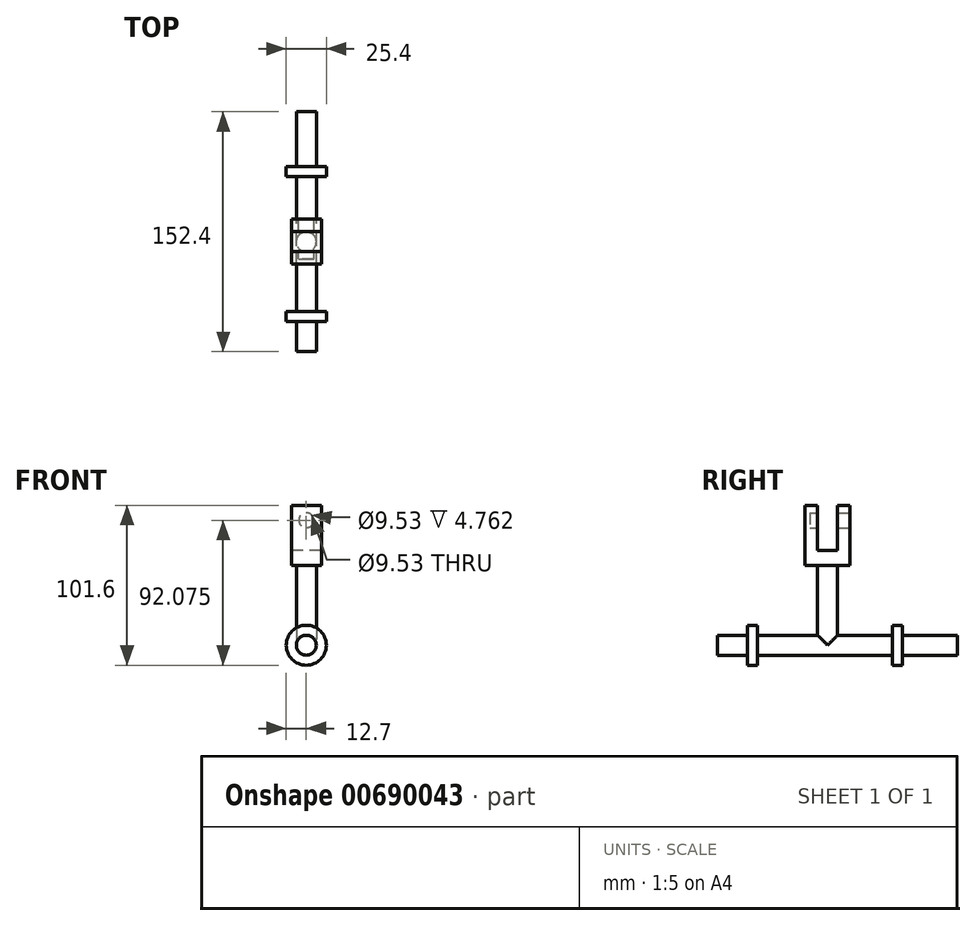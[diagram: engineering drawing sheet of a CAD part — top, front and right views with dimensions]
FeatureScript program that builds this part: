
annotation { "Feature Type Name" : "Feature", "Feature Type Description" : "" }
export const myFeature = defineFeature(function(context is Context, id is Id, definition is map)
    precondition{}
    {
        {
            var Q0;
            Q0=qCreatedBy(makeId("Front.planeOp"),FACE);
            var sketch = newSketch(context, id + "F0", { "sketchPlane" : qUnion([Q0])});
            skCircle(sketch, "E0", {"center": v(0, 0) * mm, "radius": 6.35 * mm});
            skSolve(sketch);
        }
        {
            var Q0;
            Q0 = qSketchRegion(id + "F0", true);
            extrude(context, id + "F1", {"entities" : qUnion([Q0]), "depth" : 152.4 * mm, "offsetDistance" : 25.4 * mm});
        }
        {
            var Q0;
            Q0=makeQuery(id+"F1.opExtrude","CAP_FACE",FACE,{"disambiguationData":[OSD([sQuery(id+"F0.wireOp",EDGE,"E0")])],"isStart":false});
            cPlane(context, id + "F2", {"entities" : qUnion([Q0]), "cplaneType" : CPlaneType.OFFSET, "offset" : 25.4 * mm, "oppositeDirection" : true, "width" : 152.4 * mm, "height" : 152.4 * mm});
        }
        {
            var Q0;
            Q0=qCreatedBy(id+"F2.planeOp",FACE);
            cPlane(context, id + "F3", {"entities" : qUnion([Q0]), "cplaneType" : CPlaneType.OFFSET, "offset" : 92.07 * mm, "oppositeDirection" : true, "width" : 152.4 * mm, "height" : 152.4 * mm});
        }
        {
            var Q0;
            Q0=qCreatedBy(id+"F2.planeOp",FACE);
            var sketch = newSketch(context, id + "F4", { "sketchPlane" : qUnion([Q0])});
            skCircle(sketch, "E1", {"center": v(0, 0) * mm, "radius": 12.7 * mm});
            skSolve(sketch);
        }
        {
            var Q0;
            Q0 = qSketchRegion(id + "F4", true);
            extrude(context, id + "F5", {"entities" : qUnion([Q0]), "operationType" : NewBodyOperationType.ADD, "depth" : 6.35 * mm, "offsetDistance" : 25.4 * mm});
        }
        {
            var Q0;
            Q0=qCreatedBy(id+"F3.planeOp",FACE);
            var sketch = newSketch(context, id + "F6", { "sketchPlane" : qUnion([Q0])});
            skCircle(sketch, "E2", {"center": v(0, 0) * mm, "radius": 12.7 * mm});
            skSolve(sketch);
        }
        {
            var Q0;
            Q0 = qSketchRegion(id + "F6", true);
            extrude(context, id + "F7", {"entities" : qUnion([Q0]), "operationType" : NewBodyOperationType.ADD, "depth" : 6.35 * mm, "offsetDistance" : 25.4 * mm});
        }
        {
            var Q0;
            Q0=qCreatedBy(makeId("Top.planeOp"),FACE);
            cPlane(context, id + "F8", {"entities" : qUnion([Q0]), "cplaneType" : CPlaneType.OFFSET, "offset" : 0 * mm, "width" : 152.4 * mm, "height" : 152.4 * mm});
        }
        {
            var Q0;
            Q0=qCreatedBy(id+"F8.planeOp",FACE);
            var sketch = newSketch(context, id + "F9", { "sketchPlane" : qUnion([Q0])});
            skLineSegment(sketch, "E3", {"start": v(0, 0) * mm, "end": v(0, -82.55) * mm, "construction": true});
            skCircle(sketch, "E4", {"center": v(0, -82.55) * mm, "radius": 6.35 * mm});
            skSolve(sketch);
        }
        {
            var Q0;
            Q0 = qSketchRegion(id + "F9", true);
            extrude(context, id + "F10", {"entities" : qUnion([Q0]), "operationType" : NewBodyOperationType.ADD, "depth" : 50.8 * mm, "offsetDistance" : 25.4 * mm});
        }
        {
            var Q0;
            Q0=makeQuery(id+"F10.opExtrude","CAP_FACE",FACE,{"disambiguationData":[OSD([sQuery(id+"F9.wireOp",EDGE,"E4")])],"isStart":false});
            var sketch = newSketch(context, id + "F11", { "sketchPlane" : qUnion([Q0])});
            skLineSegment(sketch, "E5.bottom", {"start": v(9.52, -68.26) * mm, "end": v(-9.52, -68.26) * mm});
            skLineSegment(sketch, "E5.top", {"start": v(9.52, -96.84) * mm, "end": v(-9.52, -96.84) * mm});
            skLineSegment(sketch, "E5.left", {"start": v(9.52, -68.26) * mm, "end": v(9.52, -96.84) * mm});
            skLineSegment(sketch, "E5.right", {"start": v(-9.52, -68.26) * mm, "end": v(-9.52, -96.84) * mm});
            skPoint(sketch, "E5.middle", {"position": v(0, -82.55) * mm});
            skSolve(sketch);
        }
        {
            var Q0;
            Q0 = qSketchRegion(id + "F11", true);
            extrude(context, id + "F12", {"entities" : qUnion([Q0]), "operationType" : NewBodyOperationType.ADD, "depth" : 38.1 * mm, "offsetDistance" : 25.4 * mm});
        }
        {
            var Q0;
            Q0=makeQuery(id+"F12.opExtrude","SWEPT_FACE",FACE,{"disambiguationData":[OSD([sQuery(id+"F11.wireOp",EDGE,"E5.right")])]});
            var sketch = newSketch(context, id + "F13", { "sketchPlane" : qUnion([Q0])});
            skLineSegment(sketch, "E6.bottom", {"start": v(76.2, 88.9) * mm, "end": v(88.9, 88.9) * mm});
            skLineSegment(sketch, "E6.top", {"start": v(76.2, 60.32) * mm, "end": v(88.9, 60.32) * mm});
            skLineSegment(sketch, "E6.left", {"start": v(76.2, 88.9) * mm, "end": v(76.2, 60.33) * mm});
            skLineSegment(sketch, "E6.right", {"start": v(88.9, 88.9) * mm, "end": v(88.9, 60.33) * mm});
            skSolve(sketch);
        }
        {
            var Q0;
            Q0 = qSketchRegion(id + "F13", true);
            extrude(context, id + "F14", {"entities" : qUnion([Q0]), "operationType" : NewBodyOperationType.REMOVE, "oppositeDirection" : true, "depth" : 25.4 * mm, "offsetDistance" : 25.4 * mm});
        }
        {
            var Q0;
            Q0=makeQuery(id+"F12.opExtrude","SWEPT_FACE",FACE,{"disambiguationData":[OSD([sQuery(id+"F11.wireOp",EDGE,"E5.bottom")])]});
            var sketch = newSketch(context, id + "F15", { "sketchPlane" : qUnion([Q0])});
            skLineSegment(sketch, "E7", {"start": v(0, 88.9) * mm, "end": v(0, 79.38) * mm, "construction": true});
            skCircle(sketch, "E8", {"center": v(0, 79.38) * mm, "radius": 4.76 * mm});
            skSolve(sketch);
        }
        {
            var Q0;
            Q0 = qSketchRegion(id + "F15", true);
            extrude(context, id + "F16", {"entities" : qUnion([Q0]), "operationType" : NewBodyOperationType.REMOVE, "oppositeDirection" : true, "depth" : 25.4 * mm, "offsetDistance" : 25.4 * mm});
        }
    });
